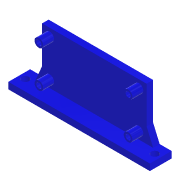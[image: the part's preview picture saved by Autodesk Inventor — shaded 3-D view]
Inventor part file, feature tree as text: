
AUTODESK INVENTOR PART (.ipt)
format: ipt  version: 2022 (Build 260153000, 153)  size: 189,440 bytes
history: native  units: mm
features: sketch x6, extrude x3, hole x2, rib x1, mirror x1, projected_geometry x1
ambient origin geometry x8: Origin, YZ Plane, XZ Plane, XY Plane, X Axis, Y Axis, Z Axis, Center Point
bodies: Solid1 (feature_tree)
feature tree (14):
  extrude  "Extrusion1"  Depth=44.0mm
  extrude  "Extrusion2"  Depth=3.0mm TaperAngle=0.0deg
  hole  "Hole1"  [1 undecoded]
  extrude  "Extrusion3"  Depth=2.0mm
  rib  "Rib2"
  hole  "Hole3"  [1 undecoded]
  mirror  "Mirror1"
  sketch  "Sketch1"  dims[d0=20.0mm d1=44.0mm]
  sketch  "Sketch2"  dims[d2=2.0mm d3=3.0mm d4=0.0mm]
  sketch  "Sketch3"  dims[d6=3.0mm d7=0.0mm d8=2.0mm]
  sketch  "Sketch6"  dims[d9=2.0mm d10=2.0mm]
  sketch  "Sketch7"  dims[d11=2.0mm]
  sketch  "Sketch8"  dims[d14=2.4mm d15=6.0mm d16=4.0mm d17=2.0mm d18=90.0deg d19=6.0mm d20=0.0mm d43=0.5mm d44=44.0mm d45=20.0mm d46=4.0mm d47=4.0mm d49=4.0mm d50=4.0mm d51=5.0mm d52=0.0mm d55=3.0mm d57=1.0mm d58=3.0mm d59=0.0mm d60=0.0mm d61=1.0mm d62=1.0mm d63=3.4mm d64=6.0mm d65=4.0mm d66=2.0mm d67=90.0deg d68=8.0mm d69=20.594885mm d70=9.0mm d71=10.0mm]
  projected_geometry  "Project Cut Edges3"
note: 2 required parameter values undecoded (feature->parameter linkage not recoverable at this tier; creation-order binding heuristic only, values carry confidence <= 0.55)
